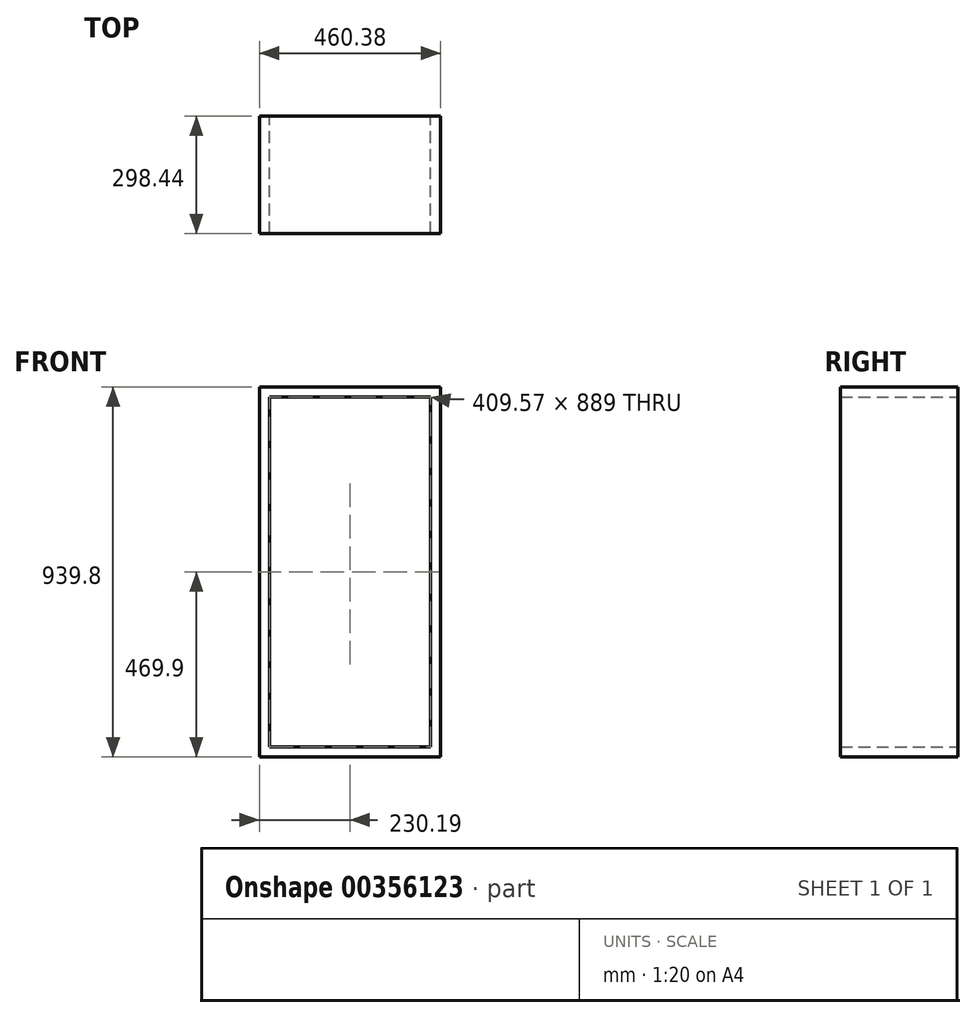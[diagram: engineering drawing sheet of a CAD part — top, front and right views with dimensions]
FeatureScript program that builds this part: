
annotation { "Feature Type Name" : "Feature", "Feature Type Description" : "" }
export const myFeature = defineFeature(function(context is Context, id is Id, definition is map)
    precondition{}
    {
        {
            var Q0;
            Q0=qCreatedBy(makeId("Front.planeOp"),FACE);
            var sketch = newSketch(context, id + "F0", { "sketchPlane" : qUnion([Q0])});
            skLineSegment(sketch, "E0.bottom", {"start": v(-230.19, 469.9) * mm, "end": v(230.19, 469.9) * mm});
            skLineSegment(sketch, "E0.top", {"start": v(-230.19, -469.9) * mm, "end": v(230.19, -469.9) * mm});
            skLineSegment(sketch, "E0.left", {"start": v(-230.19, 469.9) * mm, "end": v(-230.19, -469.9) * mm});
            skLineSegment(sketch, "E0.right", {"start": v(230.19, 469.9) * mm, "end": v(230.19, -469.9) * mm});
            skPoint(sketch, "E0.middle", {"position": v(0, 0) * mm});
            skLineSegment(sketch, "E1.0", {"start": v(-204.79, 444.5) * mm, "end": v(-204.79, -444.5) * mm});
            skLineSegment(sketch, "E1.1", {"start": v(-204.79, 444.5) * mm, "end": v(204.79, 444.5) * mm});
            skLineSegment(sketch, "E1.2", {"start": v(204.79, 444.5) * mm, "end": v(204.79, -444.5) * mm});
            skLineSegment(sketch, "E1.3", {"start": v(-204.79, -444.5) * mm, "end": v(204.79, -444.5) * mm});
            skSolve(sketch);
        }
        {
            var Q0;
            Q0=makeQuery(id+"F0.imprint","IMPRINT",FACE,{"disambiguationData":[TD([[makeQuery(id+"F0.imprint","IMPRINT",EDGE,{"derivedFrom":sQuery(id+"F0.wireOp",EDGE,"E0.bottom")}),-1.0]])]});
            extrude(context, id + "F1", {"entities" : qUnion([Q0]), "endBound" : BoundingType.SYMMETRIC, "depth" : 298.45 * mm});
        }
    });
